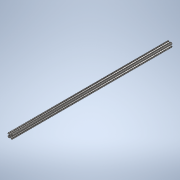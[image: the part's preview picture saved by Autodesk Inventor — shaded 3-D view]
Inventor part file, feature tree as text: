
AUTODESK INVENTOR PART (.ipt)
format: ipt  version: 2020 (Build 240168000, 168)  size: 246,272 bytes
history: native  units: in
note: dims shown in document units (in); Inventor stores cm internally (conversion verified against a paired STEP export)
features: extrude x1, sketch x1
ambient origin geometry x8: Origin, YZ Plane, XZ Plane, XY Plane, X Axis, Y Axis, Z Axis, Center Point
bodies: Solid1 (feature_tree)
feature tree (2):
  extrude  "Extrusion1"  [1 undecoded]
  sketch  "Sketch1"  dims[d0=37.0in d1=0.0in]
note: 1 required parameter value undecoded (feature->parameter linkage not recoverable at this tier; creation-order binding heuristic only, values carry confidence <= 0.55)
